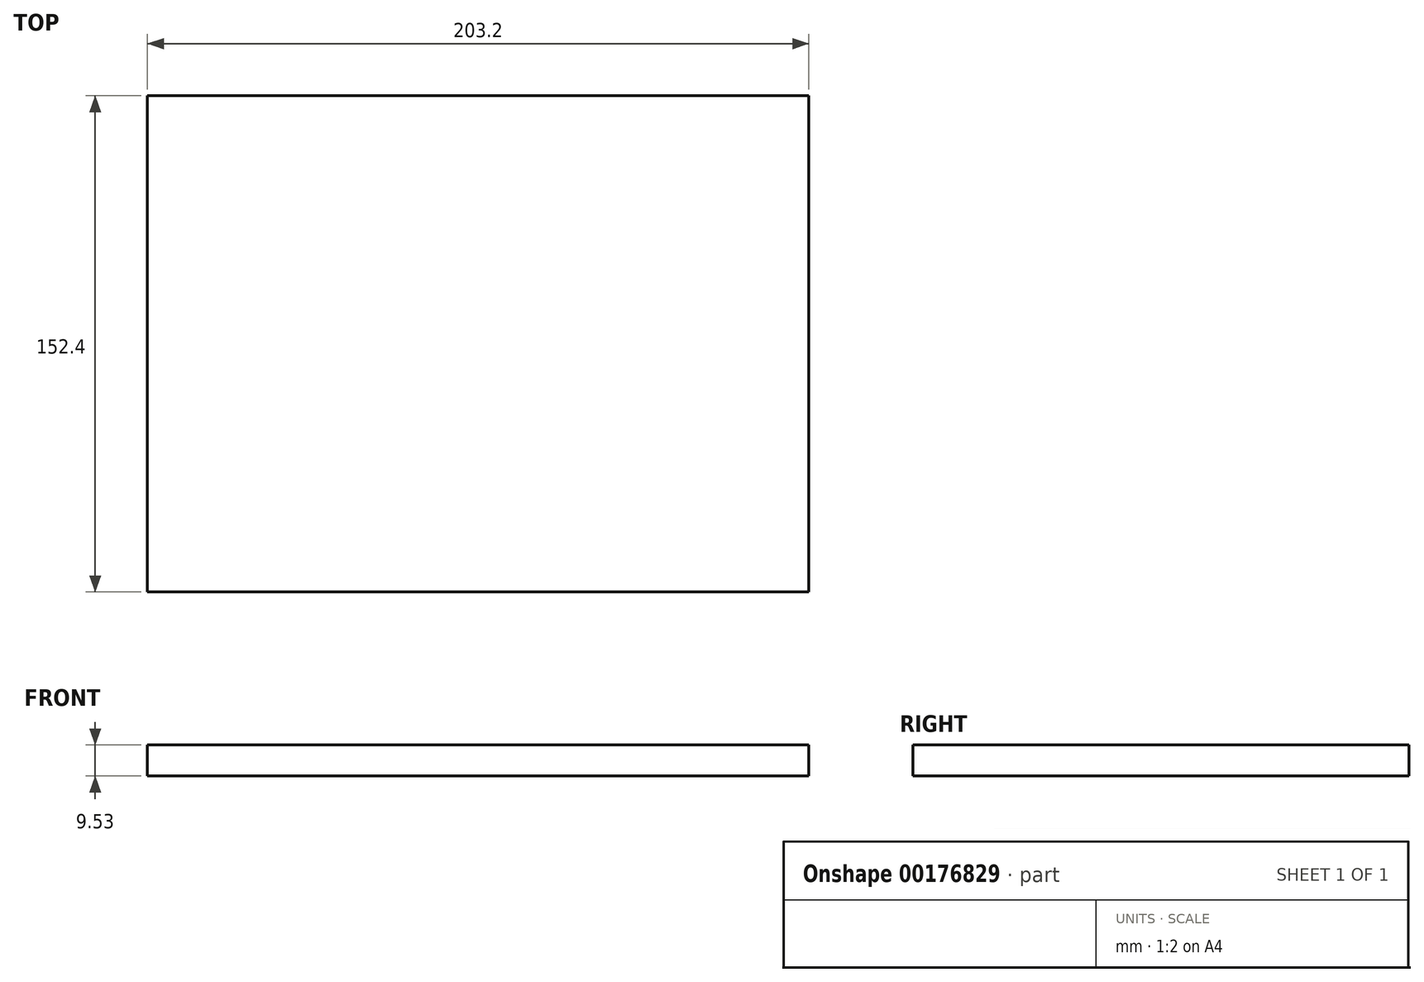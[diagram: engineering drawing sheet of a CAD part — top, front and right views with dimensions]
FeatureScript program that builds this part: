
annotation { "Feature Type Name" : "Feature", "Feature Type Description" : "" }
export const myFeature = defineFeature(function(context is Context, id is Id, definition is map)
    precondition{}
    {
        {
            var Q0;
            Q0=qCreatedBy(makeId("Top.planeOp"),FACE);
            var sketch = newSketch(context, id + "F0", { "sketchPlane" : qUnion([Q0])});
            skLineSegment(sketch, "E0.bottom", {"start": v(-71, 95.46) * mm, "end": v(132.2, 95.46) * mm});
            skLineSegment(sketch, "E0.top", {"start": v(-71, -56.94) * mm, "end": v(132.2, -56.94) * mm});
            skLineSegment(sketch, "E0.left", {"start": v(-71, 95.46) * mm, "end": v(-71, -56.94) * mm});
            skLineSegment(sketch, "E0.right", {"start": v(132.2, 95.46) * mm, "end": v(132.2, -56.94) * mm});
            skSolve(sketch);
        }
        {
            var Q0;
            Q0=makeQuery(id+"F0.imprint","IMPRINT",FACE,{"disambiguationData":[TD([[makeQuery(id+"F0.imprint","IMPRINT",EDGE,{"derivedFrom":sQuery(id+"F0.wireOp",EDGE,"E0.bottom")}),-1.0]])]});
            extrude(context, id + "F1", {"entities" : qUnion([Q0]), "depth" : 9.52 * mm});
        }
    });
